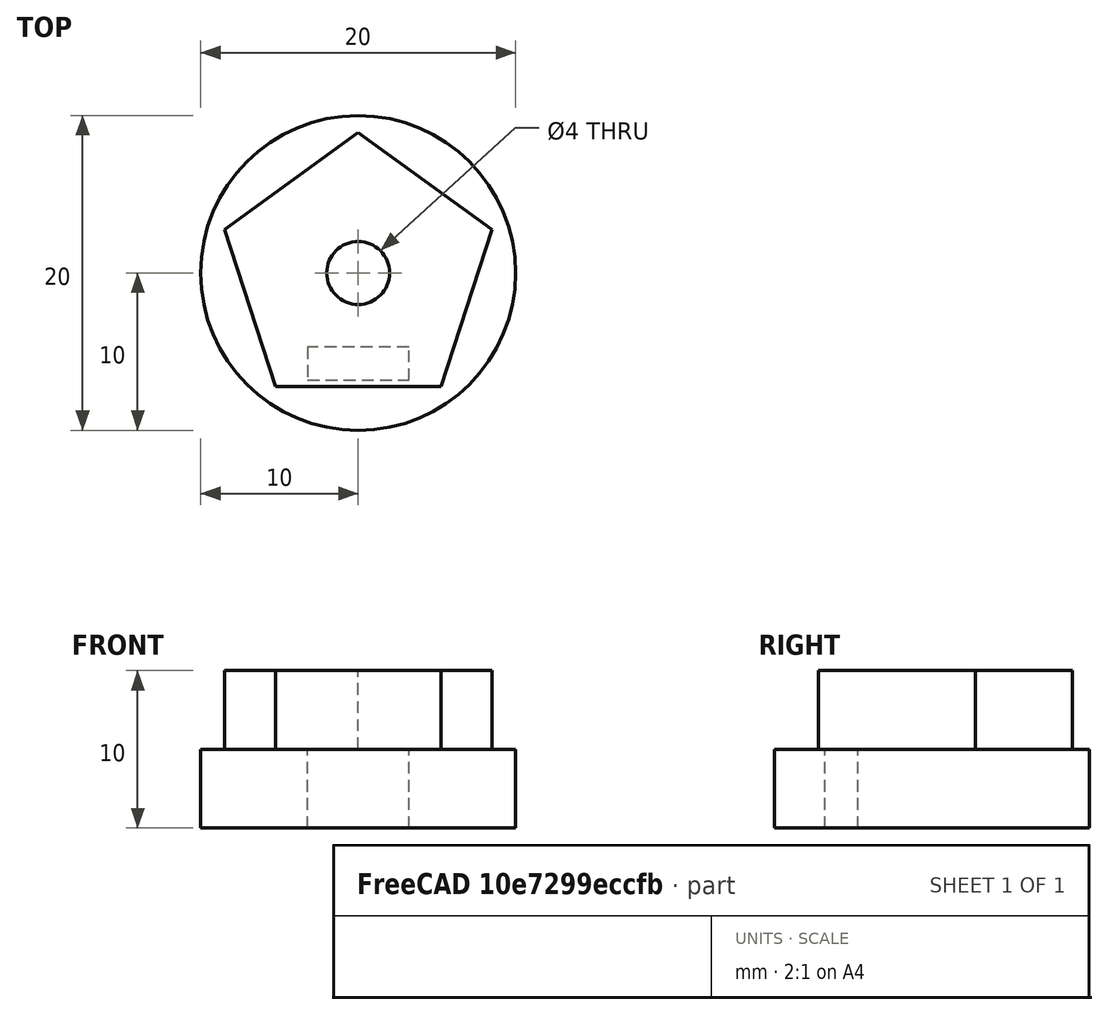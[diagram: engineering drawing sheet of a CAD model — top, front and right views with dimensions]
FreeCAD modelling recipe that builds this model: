
FCSTD DOCUMENT  (FreeCAD 0.19R)
Label: eslavon_motor
License: Creative Commons Attribution-ShareAlike
LicenseURL: http://creativecommons.org/licenses/by-sa/4.0/
objects: TechDraw::DrawViewDimension×6, Sketcher::SketchObject×4, TechDraw::DrawViewPart×4, PartDesign::Pad×2, PartDesign::Pocket×2, PartDesign::Body×1, TechDraw::DrawSVGTemplate×1, TechDraw::DrawViewBalloon×1, TechDraw::DrawPage×1
note: 13 computed .brp shape members not serialized (recipe doc carries the construction recipe); baked Part::Feature solids carry a one-line shape summary decoded from their .brp

FEATURE [Sketcher::SketchObject] Sketch
  FullyConstrained = true
  MapMode = 5
  Support = -> [XY_Plane]
  sketch-geometry (1):
    g0: Circle CenterX=0 CenterY=0 CenterZ=0 NormalX=0 NormalY=0 NormalZ=1 AngleXU=0 Radius=10
  constraints (2):
    c: Coincident(g0,g-1)
    c: Radius(g0) = 10
FEATURE [PartDesign::Pad] Pad
  Direction = (1,1,1)
  Length = 5
  Length2 = 100
  Profile = -> Sketch
  Refine = true
  Type = 0
FEATURE [Sketcher::SketchObject] Sketch001
  FullyConstrained = false
  MapMode = 5
  Placement = pos=(0,0,5) rot=(0,0,1;0rad)
  Support = -> [Pad]
  sketch-geometry (6):
    g0: LineSegment StartX=0 StartY=8.92897 StartZ=0 EndX=-8.49196 EndY=2.7592 EndZ=0
    g1: LineSegment StartX=-8.49196 StartY=2.7592 StartZ=0 EndX=-5.24832 EndY=-7.22369 EndZ=0
    g2: LineSegment StartX=-5.24832 StartY=-7.22369 StartZ=0 EndX=5.24832 EndY=-7.22369 EndZ=0
    g3: LineSegment StartX=5.24832 StartY=-7.22369 StartZ=0 EndX=8.49196 EndY=2.7592 EndZ=0
    g4: LineSegment StartX=8.49196 StartY=2.7592 StartZ=0 EndX=0 EndY=8.92897 EndZ=0
    g5: Circle CenterX=0 CenterY=0 CenterZ=0 NormalX=0 NormalY=0 NormalZ=1 AngleXU=0 Radius=8.92897
  constraints (13):
    c: Coincident(g0,g1)
    c: Coincident(g1,g2)
    c: Coincident(g2,g3)
    c: Coincident(g3,g4)
    c: Coincident(g4,g0)
    c: Equal(g0, g1-g4) x4
    c: PointOnObject(g0,g5)
    c: PointOnObject(g1,g5)
    c: PointOnObject(g2,g5)
    c: PointOnObject(g3,g5)
    c: PointOnObject(g4,g5)
    c: Coincident(g5,g-1)
    c: PointOnObject(g4,g-2)
FEATURE [PartDesign::Pad] Pad001
  BaseFeature = -> Pad
  Direction = (1,1,1)
  Length = 5
  Length2 = 100
  Profile = -> Sketch001
  Refine = true
  Type = 0
FEATURE [Sketcher::SketchObject] Sketch002
  FullyConstrained = false
  MapMode = 5
  Placement = pos=(0,0,0) rot=(1,0,0;3.14159rad)
  Support = -> [Pad001]
  sketch-geometry (4):
    g0: LineSegment StartX=-3.2147 StartY=6.81249 StartZ=0 EndX=3.2147 EndY=6.81249 EndZ=0
    g1: LineSegment StartX=3.2147 StartY=6.81249 StartZ=0 EndX=3.2147 EndY=4.6988 EndZ=0
    g2: LineSegment StartX=3.2147 StartY=4.6988 StartZ=0 EndX=-3.2147 EndY=4.6988 EndZ=0
    g3: LineSegment StartX=-3.2147 StartY=4.6988 StartZ=0 EndX=-3.2147 EndY=6.81249 EndZ=0
  constraints (8):
    c: Coincident(g0,g1)
    c: Coincident(g1,g2)
    c: Coincident(g2,g3)
    c: Coincident(g3,g0)
    c: Horizontal(g2)
    c: Vertical(g1)
    c: Vertical(g3)
    c: Symmetric(g0,g0,g-2)
FEATURE [PartDesign::Pocket] Pocket
  BaseFeature = -> Pad001
  Length = 5
  Length2 = 100
  Profile = -> Sketch002
  Refine = true
  Type = 0
FEATURE [Sketcher::SketchObject] Sketch003
  FullyConstrained = true
  MapMode = 5
  Placement = pos=(0,0,0) rot=(1,0,0;3.14159rad)
  Support = -> [Pocket]
  sketch-geometry (1):
    g0: Circle CenterX=0 CenterY=0 CenterZ=0 NormalX=0 NormalY=0 NormalZ=1 AngleXU=0 Radius=2
  constraints (2):
    c: Coincident(g0,g-1)
    c: Radius(g0) = 2
FEATURE [PartDesign::Pocket] Pocket001
  BaseFeature = -> Pocket
  Length = 5
  Length2 = 100
  Profile = -> Sketch003
  Refine = true
  Type = 1
FEATURE [PartDesign::Body] Body
  Group = -> [Sketch,Pad,Sketch001,Pad001,Sketch002,Pocket,Sketch003,Pocket001]
  Origin = -> Origin
  Tip = -> Pocket001
FEATURE [TechDraw::DrawSVGTemplate] Template002
  Height = 297
  Orientation = 1
  Width = 420
FEATURE [TechDraw::DrawViewPart] View  label="Alzado"
  CoarseView = true
  Direction = (0,-1,0)
  Focus = 100
  HardHidden = false
  IsoCount = 0
  IsoHidden = false
  IsoVisible = false
  LockPosition = true
  Perspective = false
  Rotation = 0
  Scale = 3
  ScaleType = 2
  SeamHidden = false
  SeamVisible = false
  SmoothHidden = false
  SmoothVisible = true
  Source = -> [Pocket001]
  X = 100
  XDirection = (1,0,0)
  Y = 230
FEATURE [TechDraw::DrawViewPart] View001  label="Planta"
  CoarseView = true
  Direction = (0,0,1)
  Focus = 100
  HardHidden = false
  IsoCount = 0
  IsoHidden = false
  IsoVisible = false
  LockPosition = true
  Perspective = false
  Rotation = 0
  Scale = 3
  ScaleType = 2
  SeamHidden = false
  SeamVisible = false
  SmoothHidden = false
  SmoothVisible = true
  Source = -> [Pocket001]
  X = 100
  XDirection = (1,0,0)
  Y = 120
FEATURE [TechDraw::DrawViewPart] View002  label="Perfil"
  CoarseView = true
  Direction = (1,0,0)
  Focus = 100
  HardHidden = false
  IsoCount = 0
  IsoHidden = false
  IsoVisible = false
  LockPosition = true
  Perspective = false
  Rotation = 0
  Scale = 3
  ScaleType = 2
  SeamHidden = false
  SeamVisible = false
  SmoothHidden = false
  SmoothVisible = true
  Source = -> [Pocket001]
  X = 300
  XDirection = (0,1,0)
  Y = 230
FEATURE [TechDraw::DrawViewPart] View003  label="3DView"
  CoarseView = true
  Direction = (0.57735,-0.57735,0.57735)
  Focus = 100
  HardHidden = false
  IsoCount = 0
  IsoHidden = false
  IsoVisible = false
  LockPosition = false
  Perspective = false
  Rotation = 0
  Scale = 3
  ScaleType = 2
  SeamHidden = false
  SeamVisible = false
  SmoothHidden = false
  SmoothVisible = true
  Source = -> [Pocket001]
  X = 300
  XDirection = (0.707107,0.707107,0)
  Y = 120
FEATURE [TechDraw::DrawViewDimension] Dimension
  Arbitrary = false
  ArbitraryTolerances = false
  EqualTolerance = true
  FormatSpec = %.2w
  FormatSpecOverTolerance = %+.2w
  FormatSpecUnderTolerance = %+.2w
  Inverted = false
  LockPosition = false
  MeasureType = 1
  OverTolerance = 0
  References2D = -> [View]
  Rotation = 0
  ScaleType = 0
  TheoreticalExact = false
  Type = 2
  UnderTolerance = 0
  X = 45.2749
  Y = -5
FEATURE [TechDraw::DrawViewDimension] Dimension002
  Arbitrary = false
  ArbitraryTolerances = false
  EqualTolerance = true
  FormatSpec = %.2w
  FormatSpecOverTolerance = %+.2w
  FormatSpecUnderTolerance = %+.2w
  Inverted = false
  LockPosition = false
  MeasureType = 1
  OverTolerance = 0
  References2D = -> [View]
  Rotation = 0
  ScaleType = 0
  TheoreticalExact = false
  Type = 2
  UnderTolerance = 0
  X = 40.0403
  Y = 14.618
FEATURE [TechDraw::DrawViewDimension] Dimension005
  Arbitrary = false
  ArbitraryTolerances = false
  EqualTolerance = true
  FormatSpec = %.2w
  FormatSpecOverTolerance = %+.2w
  FormatSpecUnderTolerance = %+.2w
  Inverted = false
  LockPosition = false
  MeasureType = 1
  OverTolerance = 0
  References2D = -> [View001]
  Rotation = 0
  ScaleType = 0
  TheoreticalExact = false
  Type = 1
  UnderTolerance = 0
  X = 0.302547
  Y = -43.0722
FEATURE [TechDraw::DrawViewDimension] Dimension006
  Arbitrary = false
  ArbitraryTolerances = false
  EqualTolerance = true
  FormatSpec = %.2w
  FormatSpecOverTolerance = %+.2w
  FormatSpecUnderTolerance = %+.2w
  Inverted = false
  LockPosition = false
  MeasureType = 1
  OverTolerance = 0
  References2D = -> [View002]
  Rotation = 0
  ScaleType = 0
  TheoreticalExact = false
  Type = 1
  UnderTolerance = 0
  X = -39.2924
  Y = 26.2474
FEATURE [TechDraw::DrawViewDimension] Dimension007
  Arbitrary = false
  ArbitraryTolerances = false
  EqualTolerance = true
  FormatSpec = %.2w
  FormatSpecOverTolerance = %+.2w
  FormatSpecUnderTolerance = %+.2w
  Inverted = false
  LockPosition = false
  MeasureType = 1
  OverTolerance = 0
  References2D = -> [View002]
  Rotation = 0
  ScaleType = 0
  TheoreticalExact = false
  Type = 1
  UnderTolerance = 0
  X = 42.8398
  Y = 12.3948
FEATURE [TechDraw::DrawViewDimension] Dimension008
  Arbitrary = false
  ArbitraryTolerances = false
  EqualTolerance = true
  FormatSpec = %.2w
  FormatSpecOverTolerance = %+.2w
  FormatSpecUnderTolerance = %+.2w
  Inverted = false
  LockPosition = false
  MeasureType = 1
  OverTolerance = 0
  References2D = -> [View]
  Rotation = 0
  ScaleType = 0
  TheoreticalExact = false
  Type = 1
  UnderTolerance = 0
  X = -1.21352
  Y = -30.9456
FEATURE [TechDraw::DrawViewBalloon] Balloon
  BubbleShape = 0
  EndType = 0
  EndTypeScale = 1
  KinkLength = 5
  LockPosition = false
  OriginX = 0.649676
  OriginY = 0.184289
  Rotation = 0
  ScaleType = 0
  ShapeScale = 1
  SourceView = -> View001
  Text = 4ø
  TextWrapLen = -1
  X = 14.3445
  Y = 12.3081
FEATURE [TechDraw::DrawPage] Page002  label="Planos_slave_motor"
  KeepUpdated = true
  NextBalloonIndex = 2
  ProjectionType = 0
  Template = -> Template002
  Views = -> [View,View001,View002,View003,Dimension,Dimension002,Dimension005,Dimension006,Dimension007,Dimension008,Balloon]
